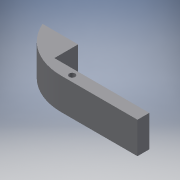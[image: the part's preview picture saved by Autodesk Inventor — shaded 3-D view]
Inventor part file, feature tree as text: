
AUTODESK INVENTOR PART (.ipt)
format: ipt  version: 2018 (Build 220112000, 112)  size: 276,992 bytes
history: native  units: mm
features: extrude x7, sketch x7, other x6, fillet x5, reference x2, plane x1, projected_geometry x1
ambient origin geometry x8: Origin, YZ Plane, XZ Plane, XY Plane, X Axis, Y Axis, Z Axis, Center Point
bodies: Solid1 (feature_tree)
feature tree (29):
  extrude  "Extrusion1"  Depth=5.0mm
  extrude  "Extrusion2"  Depth=40.0mm
  extrude  "Extrusion3"  Depth=13.3mm TaperAngle=0.0deg
  extrude  "Extrusion4"  Depth=10.0mm TaperAngle=0.0deg
  plane  "Work Plane1"
  fillet  "Fillet1"  Radius=15.0mm
  extrude  "Extrusion6"  Depth=25.0mm
  extrude  "Extrusion7"  Depth=5.0mm
  extrude  "Extrusion8"  Depth=1.5mm
  fillet  "Fillet2"  Radius=5.0mm
  fillet  "Fillet3"  Radius=3.0mm
  fillet  "Fillet4"  Radius=100.0mm
  fillet  "Fillet5"  Radius=9.5mm
  sketch  "Sketch1"  dims[d0=2.5mm d1=5.0mm]
  reference  "Reference1"
  sketch  "Sketch2"  dims[d2=40.0mm d3=65.0mm]
  reference  "Reference2"
  sketch  "Sketch3"  dims[d4=13.3mm d5=0.0mm d6=1233.0mm d7=0.0mm]
  sketch  "Sketch4"  dims[d8=10.0mm d9=1233.0mm d10=0.0mm d11=15.0mm]
  sketch  "Sketch6"  dims[d12=5.0mm d13=0.0mm d17=25.0mm]
  projected_geometry  "Projected Loop1"
  sketch  "Sketch7"  dims[d19=6.0mm d20=19.3mm d21=0.0mm d22=0.0mm d23=5.0mm]
  sketch  "Sketch8"  dims[d24=10.0mm d25=1.5mm d26=5.0mm d27=3.0mm d28=100.0mm d29=0.0mm d30=9.5mm d31=100.0mm d32=0.0mm d33=2.0mm d34=1.0mm d35=1.0mm d36=1.0mm]
  other  "<userpath>\OneDrive\Documents\Inventor\TSA\2018\Animatronics\Tortoise\Head\HeadAssembly.iam"
  other  "HeadAssembly.iam"
  other  "HeadBottom:2"
  other  "<userpath>\OneDrive\Documents\Inventor\TSA\2018\Animatronics\Tortoise\Turtle3.iam"
  other  "Turtle3.iam"
  other  "HeadBottom:1"
